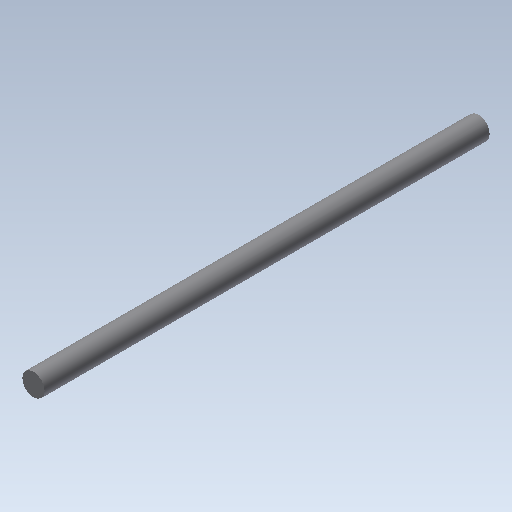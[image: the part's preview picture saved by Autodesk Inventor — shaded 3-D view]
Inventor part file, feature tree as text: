
AUTODESK INVENTOR PART (.ipt)
format: ipt  version: 2020 (Build 240168000, 168)  size: 92,672 bytes
history: native  units: in
note: dims shown in document units (in); Inventor stores cm internally (conversion verified against a paired STEP export)
features: extrude x1, other x1, imported_body x1
ambient origin geometry x8: Origin, YZ Plane, XZ Plane, XY Plane, X Axis, Y Axis, Z Axis, Center Point
bodies: Body1 (feature_tree)
feature tree (3):
  extrude  "Extrude1"  [1 undecoded]
  other  "VEX-HINGE-PIN.ipt1"
  imported_body  "Base1"
note: 1 required parameter value undecoded (feature->parameter linkage not recoverable at this tier; creation-order binding heuristic only, values carry confidence <= 0.55)
